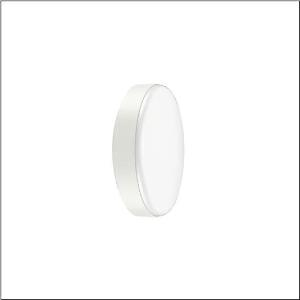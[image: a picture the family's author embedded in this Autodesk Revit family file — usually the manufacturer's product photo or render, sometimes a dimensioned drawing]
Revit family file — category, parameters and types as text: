
# Revit family: rondel_31_51wc10ma42as
name_source: partatom
category: Lighting Fixtures
units: mm (PartAtom-declared; Revit-internal decimal feet)

## family parameters
Cut with Voids When Loaded = No
Host = Face
Light Source = No
Part Type = Normal
Room Calculation Point = No
Round Connector Dimension = Use Diameter
Shared = No

## types (1)
- --- (1 x LED, 2550 lm, 20.5 W, 4000K)
    Apparent Load = 21 VA
    CIE Flux Codes = 44 75 94 94 100
    Color Rendering = 80
    Color Temperature = 4000K
    Default Elevation = 1800 mm
    Description = Rondel 31, wall and ceiling luminaire, primary optical cover: cover, of PC, opal, light emission: direct distribution, primary light characteristic: symmetric, installation type: surface-mounted, LED, rated luminous flux: 2.550lm, luminous efficacy: 124lm/W, light colour: 840, colour temperature: 4000K, with terminal, 3-pole, max. 2.5mm², mains connection: 220..240V, AC, 50/60Hz, rated input power: 20.5W, luminaire housing, of PC, traffic white (RAL 9016), diameter: 350mm, brightness and presence sensor, HF sensor, protection rating (complete): IP65, insulation class (complete): insulation class II (safety insulation), certification: CE, impact resistance: IK10, permissible operating ambient temperature: -20..+40°C, permissible storage temperature: -20..+60°C, packaging unit: 1 piece
    Height = 97 mm
    Lamp = 1 x LED
    Lamp Light Flux = 2550 lm
    Lamp Power = 20.5 W
    Lamp count = 1
    Length = 350 mm
    Luminous efficacy = 124 lm/W
    Manufacturer = Siteco
    ModVariant = No
    Model = 51WC10MA42AS
    Mounting Place = Ceiling
    Mounting Type = Surface mounted
    Number of Poles = 1
    OnlyDefault = Yes
    Power Factor = 1
    Product Name = Rondel 31
    Product group = wall and ceiling luminaire
    ProductGroupID = 302
    Protection Class = Protection class II
    Protection Degree = IP 65
    RLX_Detail_Level = 1
    RLX_Emergency_Light_Flux = 0 lm
    RLX_Emergency_Type = 0
    RLX_Emergency_Type_DB = No
    RlxData = <blob elided: 30465 chars, md5=e91ed4b9>
    Socket = socket
    Standby Power = 0 W
    System Light Flux = 2550 lm
    System Power = 21 W
    Type Comments = factory setting: luminous flux: 100 % | (ON | ON)
    Type Image = l_1007027.jpg
    URL = http://relux.com
    VarID = @adj_101001
    Voltage = 0 V
    Weight = 0.00 kg
    Width = 0 mm  [stored 0 ft]

note: [stored X ft] marks values corroborated as IEEE doubles in the binary element streams (Revit-internal decimal feet)

## geometry (parser evidence)
native form markers: Blend x4, Sweep x12
no freeform markers — native parametric forms only
